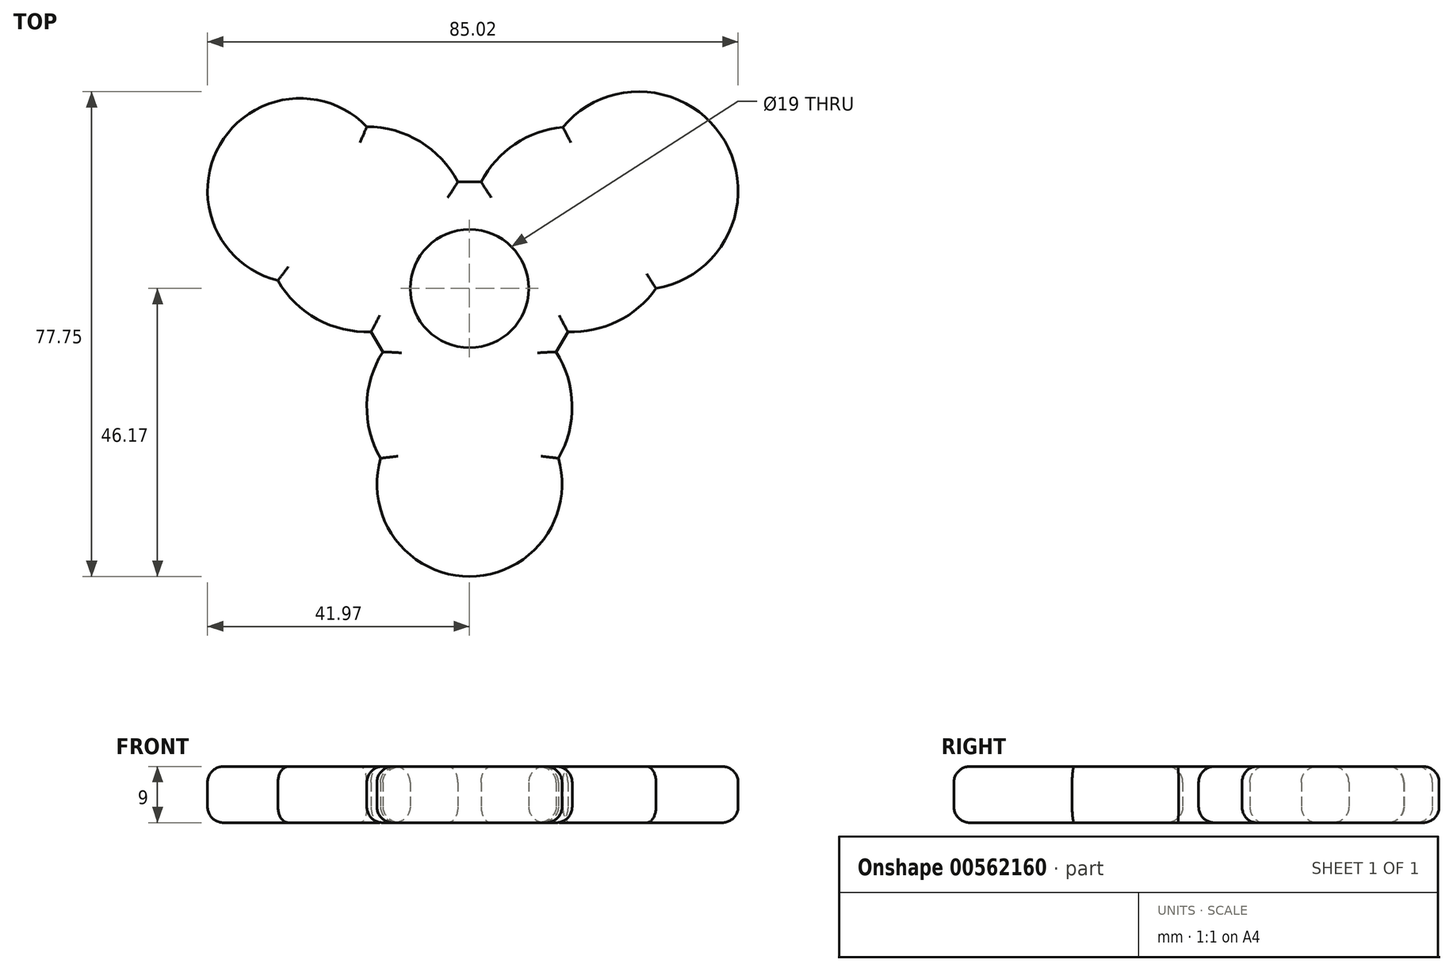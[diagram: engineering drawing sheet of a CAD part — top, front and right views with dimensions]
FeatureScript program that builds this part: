
annotation { "Feature Type Name" : "Feature", "Feature Type Description" : "" }
export const myFeature = defineFeature(function(context is Context, id is Id, definition is map)
    precondition{}
    {
        {
            var Q0;
            Q0=qCreatedBy(makeId("Top.planeOp"),FACE);
            var sketch = newSketch(context, id + "F0", { "sketchPlane" : qUnion([Q0])});
            skCircle(sketch, "E0", {"center": v(0, 0) * mm, "radius": 9.5 * mm});
            skSolve(sketch);
        }
        {
            var Q0;
            Q0=qCreatedBy(makeId("Top.planeOp"),FACE);
            var sketch = newSketch(context, id + "F1", { "sketchPlane" : qUnion([Q0])});
            skLineSegment(sketch, "E1", {"start": v(0, 0) * mm, "end": v(0, 9.5) * mm, "construction": true});
            skCircle(sketch, "E2.cCircle", {"center": v(0, 0) * mm, "radius": 9.5 * mm, "construction": true});
            skLineSegment(sketch, "E2.0", {"start": v(-16.45, 9.5) * mm, "end": v(16.45, 9.5) * mm});
            skLineSegment(sketch, "E2.1", {"start": v(16.45, 9.5) * mm, "end": v(0, -19) * mm});
            skLineSegment(sketch, "E2.2", {"start": v(0, -19) * mm, "end": v(-16.45, 9.5) * mm});
            skPoint(sketch, "E2.0.midPoint", {"position": v(0, 9.5) * mm});
            skArc(sketch, "E3", {"start": v(0, 9.5) * mm, "mid": v(30.7, 17.73) * mm, "end": v(8.23, -4.75) * mm});
            skArc(sketch, "E4", {"start": v(8.23, -4.75) * mm, "mid": v(0, -35.45) * mm, "end": v(-8.23, -4.75) * mm});
            skArc(sketch, "E5", {"start": v(0, 9.5) * mm, "mid": v(-30.7, 17.73) * mm, "end": v(-8.23, -4.75) * mm});
            skLineSegment(sketch, "E6", {"start": v(-16.45, 9.5) * mm, "end": v(-30.7, 17.73) * mm});
            skLineSegment(sketch, "E7", {"start": v(16.45, 9.5) * mm, "end": v(30.7, 17.73) * mm});
            skLineSegment(sketch, "E8", {"start": v(0, -19) * mm, "end": v(0, -35.45) * mm});
            skArc(sketch, "E9", {"start": v(14.25, -27.23) * mm, "mid": v(0, -41.48) * mm, "end": v(-14.25, -27.23) * mm});
            skPoint(sketch, "E9.startSnap0", {"position": v(0, -27.23) * mm});
            skArc(sketch, "E10", {"start": v(29.89, 0) * mm, "mid": v(36.57, 21.12) * mm, "end": v(14.94, 25.89) * mm});
            skArc(sketch, "E11", {"start": v(-30.7, 1.27) * mm, "mid": v(-35.92, 20.74) * mm, "end": v(-16.45, 25.95) * mm});
            skLineSegment(sketch, "E12", {"start": v(-23.58, 13.61) * mm, "end": v(-30.7, 17.73) * mm});
            skArc(sketch, "E13", {"start": v(-30.7, 1.27) * mm, "mid": v(-39.99, 23.09) * mm, "end": v(-16.45, 25.95) * mm});
            skLineSegment(sketch, "E14", {"start": v(23.58, 13.61) * mm, "end": v(30.7, 17.73) * mm});
            skArc(sketch, "E15", {"start": v(14.94, 25.89) * mm, "mid": v(40.92, 23.63) * mm, "end": v(29.89, 0) * mm});
            skLineSegment(sketch, "E16", {"start": v(0, -27.23) * mm, "end": v(0, -35.45) * mm});
            skArc(sketch, "E17", {"start": v(-14.25, -27.23) * mm, "mid": v(0, -46.17) * mm, "end": v(14.25, -27.23) * mm});
            skLineSegment(sketch, "E18", {"start": v(0, 9.5) * mm, "end": v(0, 17.12) * mm});
            skLineSegment(sketch, "E19", {"start": v(0, 17.12) * mm, "end": v(-1.87, 17.12) * mm});
            skLineSegment(sketch, "E20", {"start": v(-1.87, 17.12) * mm, "end": v(1.87, 17.12) * mm});
            skLineSegment(sketch, "E21", {"start": v(8.23, -4.75) * mm, "end": v(14.83, -8.56) * mm});
            skLineSegment(sketch, "E22", {"start": v(14.83, -8.56) * mm, "end": v(15.76, -6.94) * mm});
            skLineSegment(sketch, "E23", {"start": v(15.76, -6.94) * mm, "end": v(13.9, -10.18) * mm});
            skLineSegment(sketch, "E24", {"start": v(-8.23, -4.75) * mm, "end": v(-14.83, -8.56) * mm});
            skLineSegment(sketch, "E25", {"start": v(-14.83, -8.56) * mm, "end": v(-13.9, -10.18) * mm});
            skLineSegment(sketch, "E26", {"start": v(-13.9, -10.18) * mm, "end": v(-15.76, -6.94) * mm});
            skSolve(sketch);
        }
        {
            var Q0;
            Q0=makeQuery(id+"F1.imprint","IMPRINT",FACE,{"disambiguationData":[TD([[makeQuery(id+"F1.imprint","IMPRINT",EDGE,{"derivedFrom":sQuery(id+"F1.wireOp",EDGE,"E11")}),1.0]])]});
            var Q1;
            {var subQ1=sQuery(id+"F1.wireOp",EDGE,"E11");Q1=makeQuery(id+"F1.imprint","IMPRINT",FACE,{"disambiguationData":[TD([[makeQuery(id+"F1.imprint","IMPRINT",EDGE,{"derivedFrom":subQ1}),-1.0]])]});}
            var Q2;
            {var subQ0=sQuery(id+"F1.wireOp",EDGE,"E6");Q2=makeQuery(id+"F1.imprint","IMPRINT",FACE,{"disambiguationData":[TD([[makeQuery(id+"F1.imprint","IMPRINT",EDGE,{"derivedFrom":subQ0}),-1.0]])]});}
            var Q3;
            {var subQ0=sQuery(id+"F1.wireOp",EDGE,"E6");Q3=makeQuery(id+"F1.imprint","IMPRINT",FACE,{"disambiguationData":[TD([[makeQuery(id+"F1.imprint","IMPRINT",EDGE,{"derivedFrom":subQ0}),1.0]])]});}
            var Q4;
            {var subQ0=sQuery(id+"F1.wireOp",EDGE,"E2.2");var subQ6=sQuery(id+"F1.wireOp",EDGE,"E2.0");var subQ10=makeQuery(id+"F1.imprint","INTERSECT",VERTEX,{"derivedFrom":[subQ6,subQ0,sQuery(id+"F1.wireOp",EDGE,"E6")]});Q4=makeQuery(id+"F1.imprint","IMPRINT",FACE,{"disambiguationData":[TD([[makeQuery(id+"F1.imprint","IMPRINT",EDGE,{"disambiguationData":[TD([[subQ10,-1.0]])],"derivedFrom":subQ6}),-1.0]])]});}
            var Q5;
            {var subQ0=sQuery(id+"F1.wireOp",EDGE,"E7");Q5=makeQuery(id+"F1.imprint","IMPRINT",FACE,{"disambiguationData":[TD([[makeQuery(id+"F1.imprint","IMPRINT",EDGE,{"derivedFrom":subQ0}),1.0]])]});}
            var Q6;
            {var subQ0=sQuery(id+"F1.wireOp",EDGE,"E7");Q6=makeQuery(id+"F1.imprint","IMPRINT",FACE,{"disambiguationData":[TD([[makeQuery(id+"F1.imprint","IMPRINT",EDGE,{"derivedFrom":subQ0}),-1.0]])]});}
            var Q7;
            {var subQ1=sQuery(id+"F1.wireOp",EDGE,"E10");Q7=makeQuery(id+"F1.imprint","IMPRINT",FACE,{"disambiguationData":[TD([[makeQuery(id+"F1.imprint","IMPRINT",EDGE,{"derivedFrom":subQ1}),1.0]])]});}
            var Q8;
            Q8=makeQuery(id+"F1.imprint","IMPRINT",FACE,{"disambiguationData":[TD([[makeQuery(id+"F1.imprint","IMPRINT",EDGE,{"derivedFrom":sQuery(id+"F1.wireOp",EDGE,"E10")}),-1.0]])]});
            var Q9;
            {var subQ3=sQuery(id+"F1.wireOp",EDGE,"E8");Q9=makeQuery(id+"F1.imprint","IMPRINT",FACE,{"disambiguationData":[TD([[makeQuery(id+"F1.imprint","IMPRINT",EDGE,{"derivedFrom":subQ3}),1.0]])]});}
            var Q10;
            {var subQ1=sQuery(id+"F1.wireOp",EDGE,"E9");Q10=makeQuery(id+"F1.imprint","IMPRINT",FACE,{"disambiguationData":[TD([[makeQuery(id+"F1.imprint","IMPRINT",EDGE,{"derivedFrom":subQ1}),-1.0]])]});}
            var Q11;
            Q11=makeQuery(id+"F1.imprint","IMPRINT",FACE,{"disambiguationData":[TD([[makeQuery(id+"F1.imprint","IMPRINT",EDGE,{"derivedFrom":sQuery(id+"F1.wireOp",EDGE,"E9")}),1.0]])]});
            var Q12;
            {var subQ0=sQuery(id+"F1.wireOp",EDGE,"E8");Q12=makeQuery(id+"F1.imprint","IMPRINT",FACE,{"disambiguationData":[TD([[makeQuery(id+"F1.imprint","IMPRINT",EDGE,{"derivedFrom":subQ0}),-1.0]])]});}
            var Q13;
            {var subQ0=sQuery(id+"F1.wireOp",EDGE,"E24");Q13=makeQuery(id+"F1.imprint","IMPRINT",FACE,{"disambiguationData":[TD([[makeQuery(id+"F1.imprint","IMPRINT",EDGE,{"derivedFrom":subQ0}),-1.0]])]});}
            var Q14;
            {var subQ0=sQuery(id+"F1.wireOp",EDGE,"E24");Q14=makeQuery(id+"F1.imprint","IMPRINT",FACE,{"disambiguationData":[TD([[makeQuery(id+"F1.imprint","IMPRINT",EDGE,{"derivedFrom":subQ0}),1.0]])]});}
            var Q15;
            {var subQ0=sQuery(id+"F1.wireOp",EDGE,"E18");Q15=makeQuery(id+"F1.imprint","IMPRINT",FACE,{"disambiguationData":[TD([[makeQuery(id+"F1.imprint","IMPRINT",EDGE,{"derivedFrom":subQ0}),1.0]])]});}
            var Q16;
            {var subQ0=sQuery(id+"F1.wireOp",EDGE,"E21");Q16=makeQuery(id+"F1.imprint","IMPRINT",FACE,{"disambiguationData":[TD([[makeQuery(id+"F1.imprint","IMPRINT",EDGE,{"derivedFrom":subQ0}),1.0]])]});}
            var Q17;
            {var subQ0=sQuery(id+"F1.wireOp",EDGE,"E21");Q17=makeQuery(id+"F1.imprint","IMPRINT",FACE,{"disambiguationData":[TD([[makeQuery(id+"F1.imprint","IMPRINT",EDGE,{"derivedFrom":subQ0}),-1.0]])]});}
            var Q18;
            {var subQ0=sQuery(id+"F1.wireOp",EDGE,"E18");Q18=makeQuery(id+"F1.imprint","IMPRINT",FACE,{"disambiguationData":[TD([[makeQuery(id+"F1.imprint","IMPRINT",EDGE,{"derivedFrom":subQ0}),-1.0]])]});}
            extrude(context, id + "F2", {"entities" : qUnion([Q0, Q1, Q2, Q3, Q4, Q5, Q6, Q7, Q8, Q9, Q10, Q11, Q12, Q13, Q14, Q15, Q16, Q17, Q18]), "depth" : 9 * mm, "offsetDistance" : 25.4 * mm});
        }
        {
            var Q0;
            Q0=makeQuery(id+"F0.imprint","IMPRINT",FACE,{"disambiguationData":[TD([[makeQuery(id+"F0.imprint","IMPRINT",EDGE,{"derivedFrom":sQuery(id+"F0.wireOp",EDGE,"E0")}),1.0]])]});
            extrude(context, id + "F3", {"entities" : qUnion([Q0]), "operationType" : NewBodyOperationType.REMOVE, "depth" : 25.4 * mm, "offsetDistance" : 25.4 * mm});
        }
        {
            var Q0;
            {var subQ0=sQuery(id+"F1.wireOp",EDGE,"E5");var subQ1=sQuery(id+"F1.wireOp",EDGE,"E3");var subQ2=sQuery(id+"F1.wireOp",EDGE,"E13");var subQ4=sQuery(id+"F1.wireOp",EDGE,"E4");Q0=makeQuery(id+"F3.boolean.opBoolean","SPLIT",FACE,{"disambiguationData":[TD([makeQuery(id+"F2.opExtrude","SWEPT_FACE",FACE,{"disambiguationData":[OSD([subQ2])]})])],"derivedFrom":makeQuery(id+"F2.opExtrude","CAP_FACE",FACE,{"disambiguationData":[OSD([subQ1,subQ4,subQ0,subQ2,sQuery(id+"F1.wireOp",EDGE,"E15"),sQuery(id+"F1.wireOp",EDGE,"E17")])],"isStart":false})});}
            var Q1;
            {var subQ0=sQuery(id+"F1.wireOp",EDGE,"E5");var subQ1=sQuery(id+"F1.wireOp",EDGE,"E3");var subQ2=sQuery(id+"F1.wireOp",EDGE,"E15");var subQ4=sQuery(id+"F1.wireOp",EDGE,"E4");Q1=makeQuery(id+"F3.boolean.opBoolean","SPLIT",FACE,{"disambiguationData":[TD([makeQuery(id+"F2.opExtrude","SWEPT_FACE",FACE,{"disambiguationData":[OSD([subQ2])]})])],"derivedFrom":makeQuery(id+"F2.opExtrude","CAP_FACE",FACE,{"disambiguationData":[OSD([subQ1,subQ4,subQ0,sQuery(id+"F1.wireOp",EDGE,"E13"),subQ2,sQuery(id+"F1.wireOp",EDGE,"E17")])],"isStart":false})});}
            var Q2;
            {var subQ0=sQuery(id+"F1.wireOp",EDGE,"E4");var subQ1=sQuery(id+"F1.wireOp",EDGE,"E3");var subQ2=sQuery(id+"F1.wireOp",EDGE,"E17");var subQ4=sQuery(id+"F1.wireOp",EDGE,"E5");Q2=makeQuery(id+"F3.boolean.opBoolean","SPLIT",FACE,{"disambiguationData":[TD([makeQuery(id+"F2.opExtrude","SWEPT_FACE",FACE,{"disambiguationData":[OSD([subQ2])]})])],"derivedFrom":makeQuery(id+"F2.opExtrude","CAP_FACE",FACE,{"disambiguationData":[OSD([subQ1,subQ0,subQ4,sQuery(id+"F1.wireOp",EDGE,"E13"),sQuery(id+"F1.wireOp",EDGE,"E15"),subQ2])],"isStart":false})});}
            var Q3;
            Q3=makeQuery(id+"F2.opExtrude","CAP_EDGE",EDGE,{"disambiguationData":[OSD([sQuery(id+"F1.wireOp",EDGE,"E17")])],"isStart":true});
            var Q4;
            {var subQ0=sQuery(id+"F1.wireOp",EDGE,"E4");var subQ1=sQuery(id+"F1.wireOp",EDGE,"E3");var subQ2=sQuery(id+"F1.wireOp",EDGE,"E17");var subQ4=sQuery(id+"F1.wireOp",EDGE,"E5");Q4=makeQuery(id+"F3.boolean.opBoolean","SPLIT",FACE,{"disambiguationData":[TD([makeQuery(id+"F2.opExtrude","SWEPT_FACE",FACE,{"disambiguationData":[OSD([subQ2])]})])],"derivedFrom":makeQuery(id+"F2.opExtrude","CAP_FACE",FACE,{"disambiguationData":[OSD([subQ1,subQ0,subQ4,sQuery(id+"F1.wireOp",EDGE,"E13"),sQuery(id+"F1.wireOp",EDGE,"E15"),subQ2])],"isStart":true})});}
            var Q5;
            {var subQ0=sQuery(id+"F1.wireOp",EDGE,"E5");var subQ1=sQuery(id+"F1.wireOp",EDGE,"E3");var subQ2=sQuery(id+"F1.wireOp",EDGE,"E13");var subQ4=sQuery(id+"F1.wireOp",EDGE,"E4");Q5=makeQuery(id+"F3.boolean.opBoolean","SPLIT",FACE,{"disambiguationData":[TD([makeQuery(id+"F2.opExtrude","SWEPT_FACE",FACE,{"disambiguationData":[OSD([subQ2])]})])],"derivedFrom":makeQuery(id+"F2.opExtrude","CAP_FACE",FACE,{"disambiguationData":[OSD([subQ1,subQ4,subQ0,subQ2,sQuery(id+"F1.wireOp",EDGE,"E15"),sQuery(id+"F1.wireOp",EDGE,"E17")])],"isStart":true})});}
            var Q6;
            {var subQ0=sQuery(id+"F1.wireOp",EDGE,"E5");var subQ1=sQuery(id+"F1.wireOp",EDGE,"E3");var subQ2=sQuery(id+"F1.wireOp",EDGE,"E15");var subQ4=sQuery(id+"F1.wireOp",EDGE,"E4");Q6=makeQuery(id+"F3.boolean.opBoolean","SPLIT",FACE,{"disambiguationData":[TD([makeQuery(id+"F2.opExtrude","SWEPT_FACE",FACE,{"disambiguationData":[OSD([subQ2])]})])],"derivedFrom":makeQuery(id+"F2.opExtrude","CAP_FACE",FACE,{"disambiguationData":[OSD([subQ1,subQ4,subQ0,sQuery(id+"F1.wireOp",EDGE,"E13"),subQ2,sQuery(id+"F1.wireOp",EDGE,"E17")])],"isStart":true})});}
            fillet(context, id + "F4", {"entities" : qUnion([Q0, Q1, Q2, Q3, Q4, Q5, Q6]), "radius" : 2.54 * mm, "tangentPropagation" : true, "allowEdgeOverflow" : false});
        }
    });
